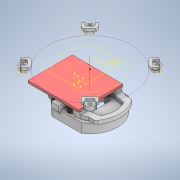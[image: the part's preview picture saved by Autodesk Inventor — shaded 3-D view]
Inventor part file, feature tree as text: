
AUTODESK INVENTOR PART (.ipt)
format: ipt  version: 2020 (Build 240168000, 168)  size: 996,864 bytes
history: native  units: mm
features: projected_geometry x32, sketch x20, extrude x15, fillet x7, other x5, chamfer x2, revolve x1, pattern_circular x1
ambient origin geometry x8: Origin, YZ Plane, XZ Plane, XY Plane, X Axis, Y Axis, Z Axis, Center Point
bodies: Body1 (feature_tree)
feature tree (83):
  other  "Твердое тело1"
  extrude  "Выдавливание1"  Depth=17.1mm
  extrude  "Выдавливание2"  Depth=17.1mm
  other  "РабПлоскость1"
  sketch  "Эскиз3"
  other  "РабОсь1"
  revolve  "Вращение1"
  extrude  "Выдавливание3"  Depth=25.0mm
  extrude  "Выдавливание4"  Depth=5.3mm
  extrude  "Выдавливание5"  Depth=44.7mm
  extrude  "Выдавливание6"  Depth=7.7mm TaperAngle=0.0deg
  extrude  "Выдавливание7"  Depth=5.0mm
  extrude  "Выдавливание8"  Depth=30.65mm
  sketch  "Эскиз10"
  extrude  "Выдавливание9"  Depth=2.5mm TaperAngle=0.0deg
  fillet  "Сопряжение1"  Radius=0.2mm
  fillet  "Сопряжение2"  [1 undecoded]
  fillet  "Сопряжение3"  Radius=1.85mm
  extrude  "Выдавливание10"  Depth=30.0mm
  fillet  "Сопряжение4"  Radius=2.0mm
  fillet  "Сопряжение5"  Radius=3.0mm
  extrude  "камера"  Depth=38.0mm
  extrude  "труба"  Depth=10.0mm TaperAngle=0.0deg
  sketch  "Эскиз15"
  other  "РабПлоскость2"
  extrude  "Выдавливание12"  Depth=5.2mm
  extrude  "Выдавливание13"  Depth=6.0mm
  chamfer  "Фаска1"  Distance=29.46mm
  fillet  "Сопряжение6"  Radius=10.0mm
  fillet  "Сопряжение7"  Radius=9.5mm
  other  "РабОсь2"
  pattern_circular  "Круговой массив1"  [2 undecoded]
  extrude  "Выдавливание15"  TaperAngle=60.0deg  [1 undecoded]
  chamfer  "Фаска2"  Distance=6.0mm
  sketch  "Эскиз20"
  sketch  "Эскиз21"
  sketch  "Эскиз1"
  sketch  "Эскиз2"
  projected_geometry  "Спроецированная петля1"
  projected_geometry  "Спроецированная петля2"
  sketch  "Эскиз4"
  projected_geometry  "Спроецированная петля3"
  sketch  "Эскиз5"
  sketch  "Эскиз6"
  projected_geometry  "Спроецированная петля4"
  sketch  "Эскиз7"
  projected_geometry  "Спроецированная петля5"
  sketch  "Эскиз8"
  projected_geometry  "Спроецированная петля6"
  projected_geometry  "Спроецированная петля7"
  projected_geometry  "Спроецированная петля8"
  sketch  "Эскиз9"
  projected_geometry  "Спроецированная петля9"
  projected_geometry  "Спроецированная петля10"
  projected_geometry  "Спроецированная петля11"
  projected_geometry  "Спроецированная петля12"
  sketch  "Эскиз11"
  sketch  "Эскиз12"
  projected_geometry  "Спроецированная петля13"
  projected_geometry  "Спроецированная петля14"
  projected_geometry  "Спроецированная петля15"
  sketch  "Эскиз14"
  projected_geometry  "Спроецированная петля20"
  projected_geometry  "Спроецированная петля21"
  projected_geometry  "Спроецированная петля22"
  projected_geometry  "Спроецированная петля23"
  sketch  "Эскиз16"
  projected_geometry  "Спроецированная петля24"
  sketch  "Эскиз17"
  projected_geometry  "Спроецированная петля25"
  sketch  "Эскиз18"
  sketch  "Эскиз19"
  projected_geometry  "Спроецированная петля26"
  projected_geometry  "Спроецированная петля27"
  projected_geometry  "Спроецированная петля28"
  projected_geometry  "Спроецированная петля29"
  projected_geometry  "Спроецированная петля30"
  projected_geometry  "Спроецированная петля31"
  projected_geometry  "Спроецированная петля32"
  projected_geometry  "Спроецированная петля33"
  projected_geometry  "Спроецированная петля34"
  projected_geometry  "Спроецированная петля35"
  projected_geometry  "Спроецированная петля36"
note: 4 required parameter values undecoded (feature->parameter linkage not recoverable at this tier; creation-order binding heuristic only, values carry confidence <= 0.55)
